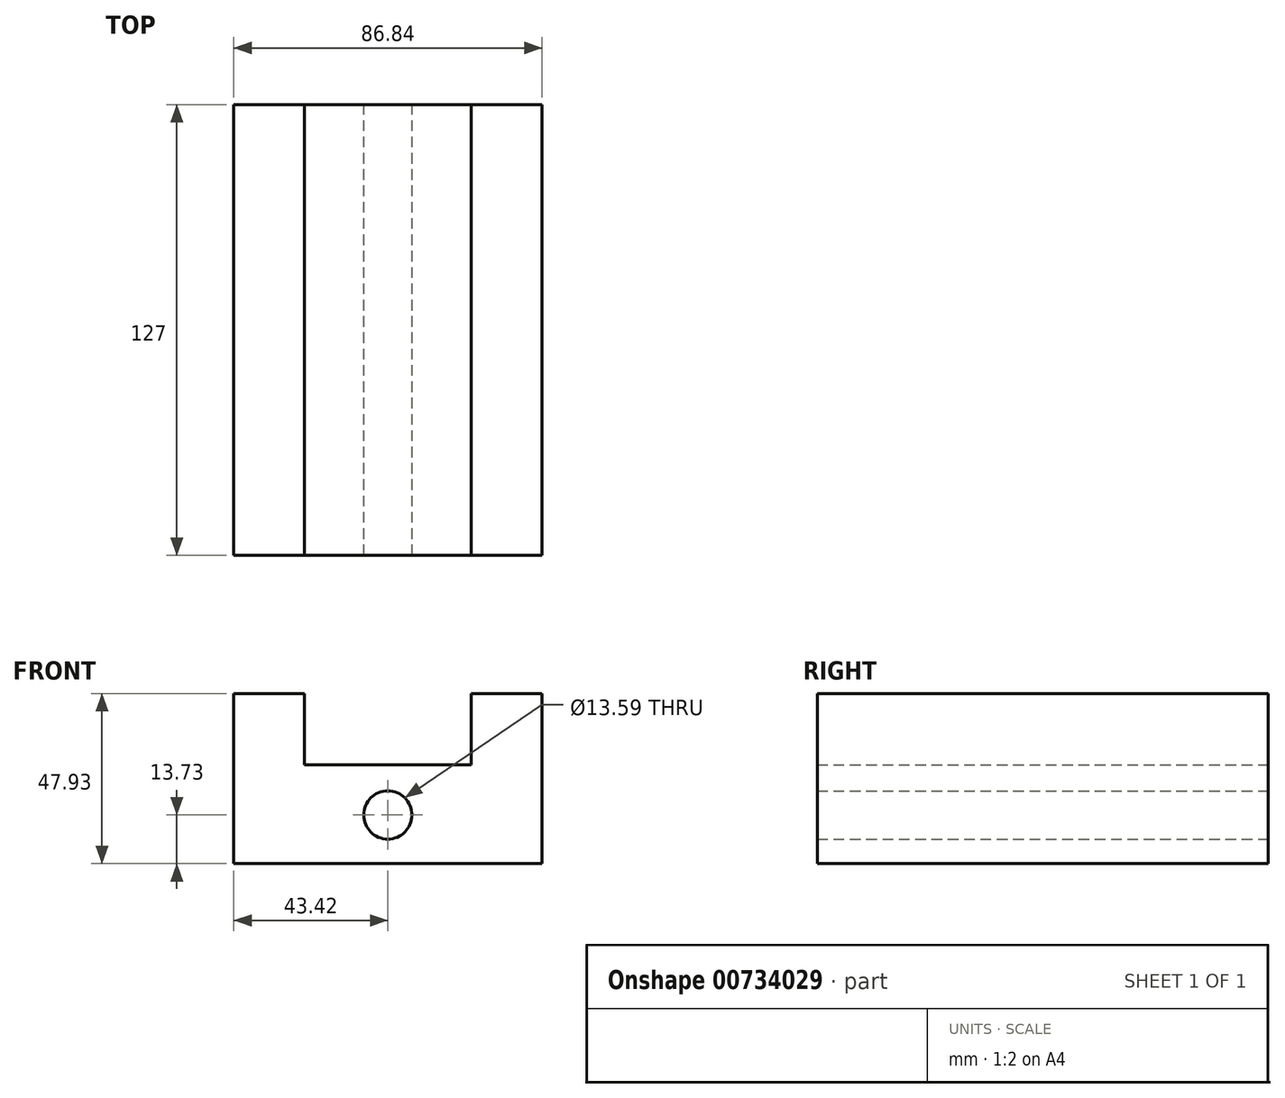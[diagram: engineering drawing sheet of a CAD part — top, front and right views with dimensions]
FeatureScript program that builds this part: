
annotation { "Feature Type Name" : "Feature", "Feature Type Description" : "" }
export const myFeature = defineFeature(function(context is Context, id is Id, definition is map)
    precondition{}
    {
        {
            var Q0;
            Q0=qCreatedBy(makeId("Front.planeOp"),FACE);
            var sketch = newSketch(context, id + "F0", { "sketchPlane" : qUnion([Q0])});
            skLineSegment(sketch, "E0.bottom", {"start": v(-43.42, 14.1) * mm, "end": v(43.42, 14.1) * mm});
            skLineSegment(sketch, "E0.top", {"start": v(-43.42, -13.73) * mm, "end": v(43.42, -13.73) * mm});
            skLineSegment(sketch, "E0.left", {"start": v(-43.42, 14.1) * mm, "end": v(-43.42, -13.73) * mm});
            skLineSegment(sketch, "E0.right", {"start": v(43.42, 14.1) * mm, "end": v(43.42, -13.73) * mm});
            skLineSegment(sketch, "E1.bottom", {"start": v(-43.42, 14.1) * mm, "end": v(-23.5, 14.1) * mm});
            skLineSegment(sketch, "E1.top", {"start": v(-43.42, 34.2) * mm, "end": v(-23.5, 34.2) * mm});
            skLineSegment(sketch, "E1.left", {"start": v(-43.42, 14.1) * mm, "end": v(-43.42, 34.2) * mm});
            skLineSegment(sketch, "E1.right", {"start": v(-23.5, 14.1) * mm, "end": v(-23.5, 34.2) * mm});
            skLineSegment(sketch, "E2.MirrorCS", {"start": v(43.42, 34.2) * mm, "end": v(23.5, 34.2) * mm});
            skLineSegment(sketch, "E3.MirrorCS", {"start": v(43.42, 14.1) * mm, "end": v(43.42, 34.2) * mm});
            skLineSegment(sketch, "E4.MirrorCS", {"start": v(23.5, 14.1) * mm, "end": v(23.5, 34.2) * mm});
            skLineSegment(sketch, "E5.MirrorCS", {"start": v(43.42, 14.1) * mm, "end": v(23.5, 14.1) * mm});
            skCircle(sketch, "E6", {"center": v(0, 0) * mm, "radius": 6.8 * mm});
            skLineSegment(sketch, "E7.bottom", {"start": v(-41.03, -26.7) * mm, "end": v(27.6, -26.7) * mm});
            skLineSegment(sketch, "E7.top", {"start": v(-41.03, -47.53) * mm, "end": v(27.6, -47.53) * mm});
            skLineSegment(sketch, "E7.left", {"start": v(-41.03, -26.7) * mm, "end": v(-41.03, -47.53) * mm});
            skLineSegment(sketch, "E7.right", {"start": v(27.6, -26.7) * mm, "end": v(27.6, -47.53) * mm});
            skLineSegment(sketch, "E8.bottom", {"start": v(-20.2, -47.53) * mm, "end": v(10.05, -47.53) * mm});
            skLineSegment(sketch, "E8.top", {"start": v(-20.2, -68.36) * mm, "end": v(10.05, -68.36) * mm});
            skLineSegment(sketch, "E8.left", {"start": v(-20.2, -47.53) * mm, "end": v(-20.2, -68.36) * mm});
            skLineSegment(sketch, "E8.right", {"start": v(10.05, -47.53) * mm, "end": v(10.05, -68.36) * mm});
            skSolve(sketch);
        }
        {
            var Q0;
            Q0=makeQuery(id+"F0.imprint","IMPRINT",FACE,{"disambiguationData":[TD([[makeQuery(id+"F0.imprint","IMPRINT",EDGE,{"derivedFrom":sQuery(id+"F0.wireOp",EDGE,"E1.top")}),-1.0]])]});
            var Q1;
            Q1=makeQuery(id+"F0.imprint","IMPRINT",FACE,{"disambiguationData":[TD([[makeQuery(id+"F0.imprint","IMPRINT",EDGE,{"derivedFrom":sQuery(id+"F0.wireOp",EDGE,"E0.top")}),1.0]])]});
            var Q2;
            Q2=makeQuery(id+"F0.imprint","IMPRINT",FACE,{"disambiguationData":[TD([[makeQuery(id+"F0.imprint","IMPRINT",EDGE,{"derivedFrom":sQuery(id+"F0.wireOp",EDGE,"E2.MirrorCS")}),1.0]])]});
            extrude(context, id + "F1", {"entities" : qUnion([Q0, Q1, Q2]), "endBound" : BoundingType.SYMMETRIC, "depth" : 127 * mm, "offsetDistance" : 25.4 * mm});
        }
    });
